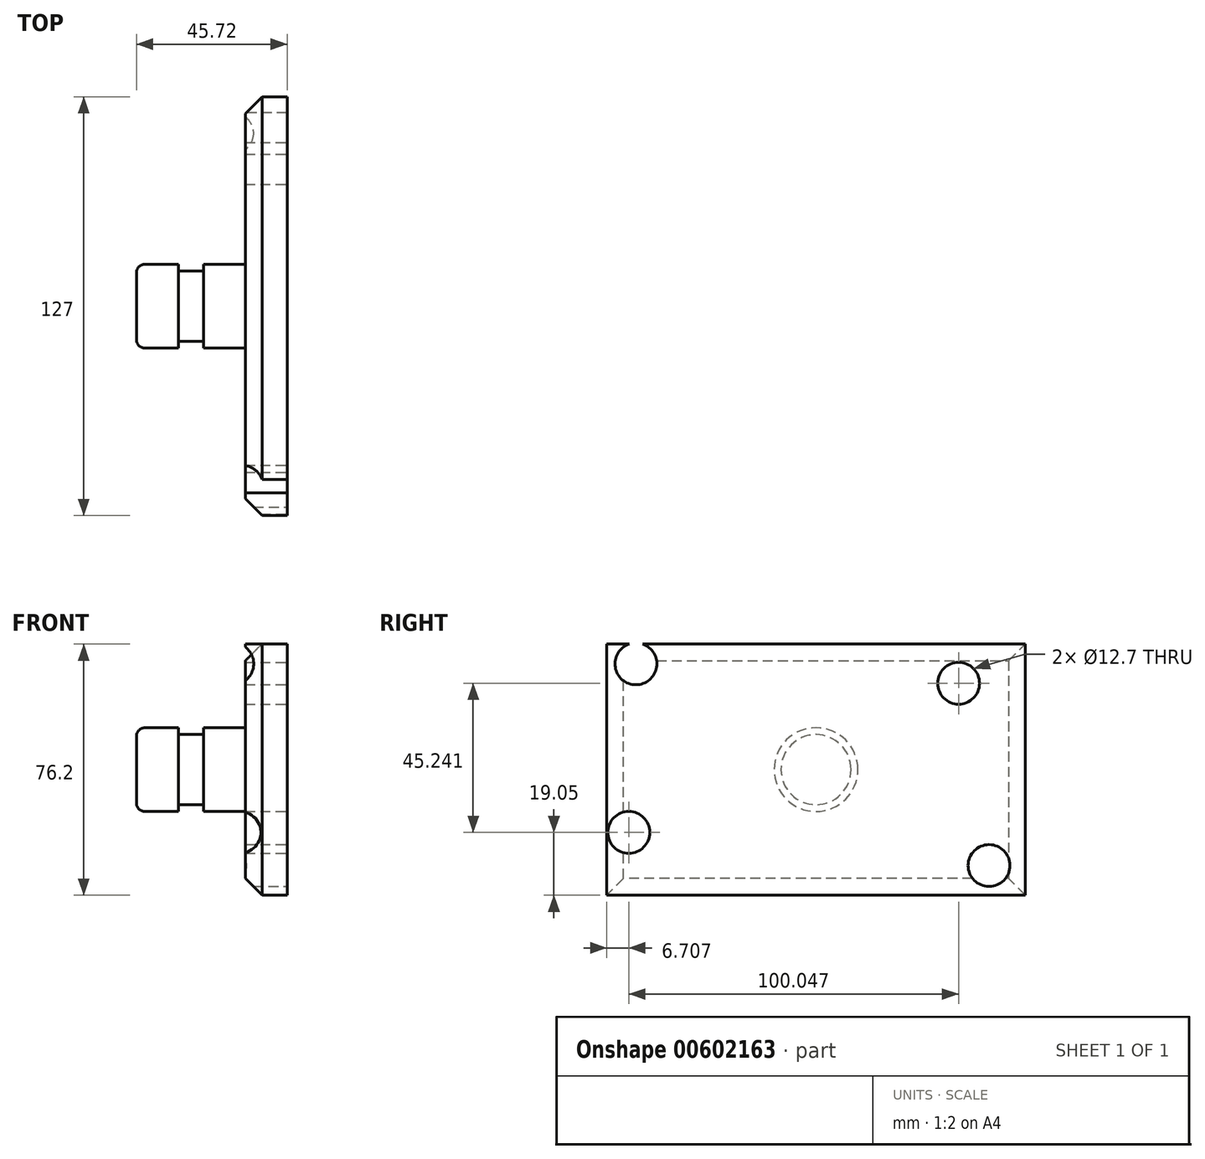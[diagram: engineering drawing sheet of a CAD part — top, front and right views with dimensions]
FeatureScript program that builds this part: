
annotation { "Feature Type Name" : "Feature", "Feature Type Description" : "" }
export const myFeature = defineFeature(function(context is Context, id is Id, definition is map)
    precondition{}
    {
        {
            var Q0;
            Q0=qCreatedBy(makeId("Right.planeOp"),FACE);
            var sketch = newSketch(context, id + "F0", { "sketchPlane" : qUnion([Q0])});
            skLineSegment(sketch, "E0.bottom", {"start": v(63.5, -38.1) * mm, "end": v(-63.5, -38.1) * mm});
            skLineSegment(sketch, "E0.top", {"start": v(63.5, 38.1) * mm, "end": v(-63.5, 38.1) * mm});
            skLineSegment(sketch, "E0.left", {"start": v(63.5, -38.1) * mm, "end": v(63.5, 38.1) * mm});
            skLineSegment(sketch, "E0.right", {"start": v(-63.5, -38.1) * mm, "end": v(-63.5, 38.1) * mm});
            skPoint(sketch, "E0.middle", {"position": v(0, 0) * mm});
            skSolve(sketch);
        }
        {
            var Q0;
            Q0=makeQuery(id+"F0.imprint","IMPRINT",FACE,{"disambiguationData":[TD([[makeQuery(id+"F0.imprint","IMPRINT",EDGE,{"derivedFrom":sQuery(id+"F0.wireOp",EDGE,"E0.bottom")}),-1.0]])]});
            extrude(context, id + "F1", {"entities" : qUnion([Q0]), "depth" : 12.7 * mm, "offsetDistance" : 25.4 * mm});
        }
        {
            var Q0;
            Q0=makeQuery(id+"F1.opExtrude","CAP_FACE",FACE,{"disambiguationData":[OSD([sQuery(id+"F0.wireOp",EDGE,"E0.bottom"),sQuery(id+"F0.wireOp",EDGE,"E0.top"),sQuery(id+"F0.wireOp",EDGE,"E0.left"),sQuery(id+"F0.wireOp",EDGE,"E0.right")])],"isStart":false});
            var sketch = newSketch(context, id + "F2", { "sketchPlane" : qUnion([Q0])});
            skCircle(sketch, "E1", {"center": v(-54.64, 32.09) * mm, "radius": 6.35 * mm});
            skCircle(sketch, "E2", {"center": v(-56.8, -19.05) * mm, "radius": 6.35 * mm});
            skCircle(sketch, "E3", {"center": v(52.5, -29.11) * mm, "radius": 6.35 * mm});
            skCircle(sketch, "E4", {"center": v(43.25, 26.2) * mm, "radius": 6.35 * mm});
            skSolve(sketch);
        }
        {
            var Q0;
            {var subQ0=sQuery(id+"F2.wireOp",EDGE,"E2");var subQ1=makeQuery(id+"F1.opExtrude","CAP_EDGE",EDGE,{"disambiguationData":[OSD([sQuery(id+"F0.wireOp",EDGE,"E0.right")])],"isStart":false});var subQ2=makeQuery(id+"F2.imprint","INTERSECT",VERTEX,{"disambiguationData":[OD(0.0)],"derivedFrom":[subQ1,subQ0]});Q0=makeQuery(id+"F2.imprint","IMPRINT",FACE,{"disambiguationData":[TD([[makeQuery(id+"F2.imprint","IMPRINT",EDGE,{"disambiguationData":[TD([[subQ2,-1.0]])],"derivedFrom":subQ0}),1.0]])]});}
            var Q1;
            {var subQ0=sQuery(id+"F2.wireOp",EDGE,"E1");var subQ1=makeQuery(id+"F1.opExtrude","CAP_EDGE",EDGE,{"disambiguationData":[OSD([sQuery(id+"F0.wireOp",EDGE,"E0.top")])],"isStart":false});var subQ2=makeQuery(id+"F2.imprint","INTERSECT",VERTEX,{"disambiguationData":[OD(0.0)],"derivedFrom":[subQ1,subQ0]});Q1=makeQuery(id+"F2.imprint","IMPRINT",FACE,{"disambiguationData":[TD([[makeQuery(id+"F2.imprint","IMPRINT",EDGE,{"disambiguationData":[TD([[subQ2,1.0]])],"derivedFrom":subQ0}),1.0]])]});}
            var Q2;
            Q2=makeQuery(id+"F2.imprint","IMPRINT",FACE,{"disambiguationData":[TD([[makeQuery(id+"F2.imprint","IMPRINT",EDGE,{"derivedFrom":sQuery(id+"F2.wireOp",EDGE,"E4")}),1.0]])]});
            var Q3;
            Q3=makeQuery(id+"F2.imprint","IMPRINT",FACE,{"disambiguationData":[TD([[makeQuery(id+"F2.imprint","IMPRINT",EDGE,{"derivedFrom":sQuery(id+"F2.wireOp",EDGE,"E3")}),1.0]])]});
            extrude(context, id + "F3", {"entities" : qUnion([Q0, Q1, Q2, Q3]), "operationType" : NewBodyOperationType.REMOVE, "endBound" : BoundingType.THROUGH_ALL, "oppositeDirection" : true, "depth" : 6.35 * mm, "offsetDistance" : 25.4 * mm});
        }
        {
            var Q0;
            Q0=qCreatedBy(makeId("Top.planeOp"),FACE);
            var sketch = newSketch(context, id + "F4", { "sketchPlane" : qUnion([Q0])});
            skLineSegment(sketch, "E5.bottom", {"start": v(-12.7, 0) * mm, "end": v(0, 0) * mm});
            skLineSegment(sketch, "E5.top", {"start": v(-12.7, -12.7) * mm, "end": v(0, -12.7) * mm});
            skLineSegment(sketch, "E5.left", {"start": v(-12.7, 0) * mm, "end": v(-12.7, -12.7) * mm});
            skLineSegment(sketch, "E5.right", {"start": v(0, 0) * mm, "end": v(0, -12.7) * mm});
            skLineSegment(sketch, "E6.bottom", {"start": v(-20.32, 0) * mm, "end": v(-12.7, 0) * mm});
            skLineSegment(sketch, "E6.top", {"start": v(-20.32, -10.63) * mm, "end": v(-12.7, -10.63) * mm});
            skLineSegment(sketch, "E6.left", {"start": v(-20.32, 0) * mm, "end": v(-20.32, -10.63) * mm});
            skLineSegment(sketch, "E6.right", {"start": v(-12.7, 0) * mm, "end": v(-12.7, -10.63) * mm});
            skPoint(sketch, "E7.firstSnap0", {"position": v(-16.5, 0) * mm});
            skLineSegment(sketch, "E7.bottom", {"start": v(-33.02, 0) * mm, "end": v(-20.32, 0) * mm});
            skLineSegment(sketch, "E7.top", {"start": v(-33.02, -12.7) * mm, "end": v(-20.32, -12.7) * mm});
            skLineSegment(sketch, "E7.left", {"start": v(-33.02, 0) * mm, "end": v(-33.02, -12.7) * mm});
            skLineSegment(sketch, "E7.right", {"start": v(-20.32, 0) * mm, "end": v(-20.32, -12.7) * mm});
            skSolve(sketch);
        }
        {
            var Q0;
            {var subQ1=sQuery(id+"F4.wireOp",EDGE,"E7.bottom");Q0=makeQuery(id+"F4.imprint","IMPRINT",FACE,{"disambiguationData":[TD([[makeQuery(id+"F4.imprint","IMPRINT",EDGE,{"derivedFrom":subQ1}),-1.0]])]});}
            var Q1;
            {var subQ0=sQuery(id+"F4.wireOp",EDGE,"E6.bottom");Q1=makeQuery(id+"F4.imprint","IMPRINT",FACE,{"disambiguationData":[TD([[makeQuery(id+"F4.imprint","IMPRINT",EDGE,{"derivedFrom":subQ0}),-1.0]])]});}
            var Q2;
            Q2=makeQuery(id+"F4.imprint","IMPRINT",FACE,{"disambiguationData":[TD([[makeQuery(id+"F4.imprint","IMPRINT",EDGE,{"derivedFrom":sQuery(id+"F4.wireOp",EDGE,"E5.bottom")}),-1.0]])]});
            var Q3;
            Q3=sQuery(id+"F4.wireOp",EDGE,"E7.bottom");
            revolve(context, id + "F5", {"operationType" : NewBodyOperationType.ADD, "entities" : qUnion([Q0, Q1, Q2]), "axis" : qUnion([Q3]), "revolveType" : RevolveType.FULL});
        }
        {
            var Q0;
            Q0=makeQuery(id+"F5.opRevolve","SWEPT_FACE",FACE,{"disambiguationData":[OSD([sQuery(id+"F4.wireOp",EDGE,"E7.left")])]});
            var Q1;
            Q1=makeQuery(id+"F5.opRevolve","SWEPT_EDGE",EDGE,{"disambiguationData":[OSD([sQuery(id+"F4.wireOp",EDGE,"E5.top"),sQuery(id+"F4.wireOp",EDGE,"E5.right")])]});
            fillet(context, id + "F6", {"entities" : qUnion([Q0, Q1]), "radius" : 2.54 * mm, "tangentPropagation" : true, "allowEdgeOverflow" : false});
        }
        {
            var Q0;
            Q0=makeQuery(id+"F1.opExtrude","CAP_EDGE",EDGE,{"disambiguationData":[OSD([sQuery(id+"F0.wireOp",EDGE,"E0.left")])],"isStart":true});
            var Q1;
            Q1=makeQuery(id+"F1.opExtrude","CAP_EDGE",EDGE,{"disambiguationData":[OSD([sQuery(id+"F0.wireOp",EDGE,"E0.bottom")])],"isStart":true});
            var Q2;
            Q2=makeQuery(id+"F1.opExtrude","CAP_EDGE",EDGE,{"disambiguationData":[OSD([sQuery(id+"F0.wireOp",EDGE,"E0.right")])],"isStart":true});
            var Q3;
            {var subQ0=sQuery(id+"F0.wireOp",EDGE,"E0.left");var subQ1=sQuery(id+"F0.wireOp",EDGE,"E0.top");Q3=makeQuery(id+"F3.boolean.opBoolean","SPLIT",EDGE,{"disambiguationData":[TD([makeQuery(id+"F1.opExtrude","SWEPT_FACE",FACE,{"disambiguationData":[OSD([subQ0])]})])],"derivedFrom":makeQuery(id+"F1.opExtrude","CAP_EDGE",EDGE,{"disambiguationData":[OSD([subQ1])],"isStart":true})});}
            chamfer(context, id + "F7", {"entities" : qUnion([Q0, Q1, Q2, Q3]), "width" : 5.08 * mm, "tangentPropagation" : true});
        }
    });
